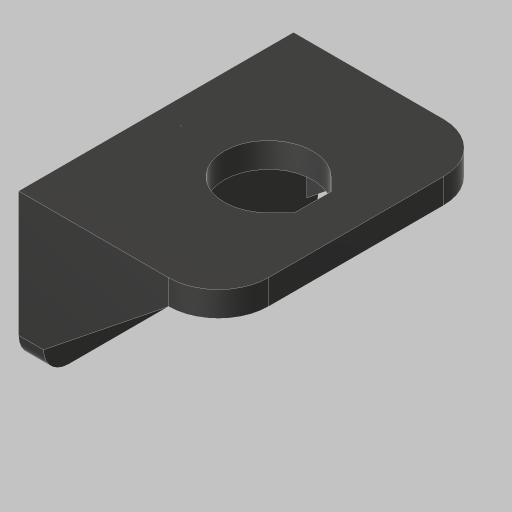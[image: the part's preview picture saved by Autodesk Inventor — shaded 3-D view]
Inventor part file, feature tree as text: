
AUTODESK INVENTOR PART (.ipt)
format: ipt  version: 2023.5 (Build 275446000, 446)  size: 211,968 bytes
history: native  units: in
note: dims shown in document units (in); Inventor stores cm internally (conversion verified against a paired STEP export)
features: sketch x7, extrude x5, projected_geometry x5, fillet x4, hole x2, mirror x1, chamfer x1
ambient origin geometry x8: Origin, YZ Plane, XZ Plane, XY Plane, X Axis, Y Axis, Z Axis, Center Point
bodies: Solid1 (feature_tree)
feature tree (25):
  extrude  "Extrusion1"  Depth=1.5in
  sketch  "Sketch2"  dims[d2=0.25in d3=0.25in]
  hole  "Hole1"  [1 undecoded]
  extrude  "Extrusion2"  Depth=0.5in
  fillet  "Fillet1"  Radius=2.0in
  fillet  "Fillet2"  Radius=0.5in
  fillet  "Fillet3"  Radius=0.126in
  extrude  "Extrusion3"  TaperAngle=0.0deg  [1 undecoded]
  mirror  "Mirror1"
  fillet  "Fillet4"  Radius=0.0315in
  extrude  "Extrusion4"  Depth=0.25in
  sketch  "Sketch7"  dims[d21=0.5in d22=0.25in]
  sketch  "Sketch8"  dims[d23=0.1181in d24=0.0in d25=0.125in d26=0.125in d27=45.0deg d28=0.25in d29=0.3in d30=1.1743in d31=0.0in d32=0.0in d33=0.201in d34=0.75in d35=0.385in d36=0.25in d37=0.5635in d38=1.0in d39=0.8108in d40=1.0in d41=0.0in d42=0.0625in d43=0.75in d44=0.375in]
  hole  "Hole2"  [1 undecoded]
  extrude  "Extrusion5"  Depth=0.25in
  chamfer  "Chamfer1"  Distance=0.3in
  sketch  "Sketch1"  dims[d0=2.0in d1=1.5in]
  projected_geometry  "Projected Loop1"
  sketch  "Sketch3"  dims[d4=2.75in d5=0.0in d6=0.886in d7=2.0in d8=0.5in]
  projected_geometry  "Projected Loop2"
  projected_geometry  "Projected Loop3"
  sketch  "Sketch5"  dims[d9=0.201in d10=0.236in d11=0.385in d12=0.25in d13=0.5635in d14=1.0in d15=0.8108in d16=0.126in]
  projected_geometry  "Projected Loop4"
  sketch  "Sketch6"  dims[d17=0.5098in d18=0.0in d19=0.0in d20=0.0315in]
  projected_geometry  "Project Cut Edges1"
note: 3 required parameter values undecoded (feature->parameter linkage not recoverable at this tier; creation-order binding heuristic only, values carry confidence <= 0.55)
